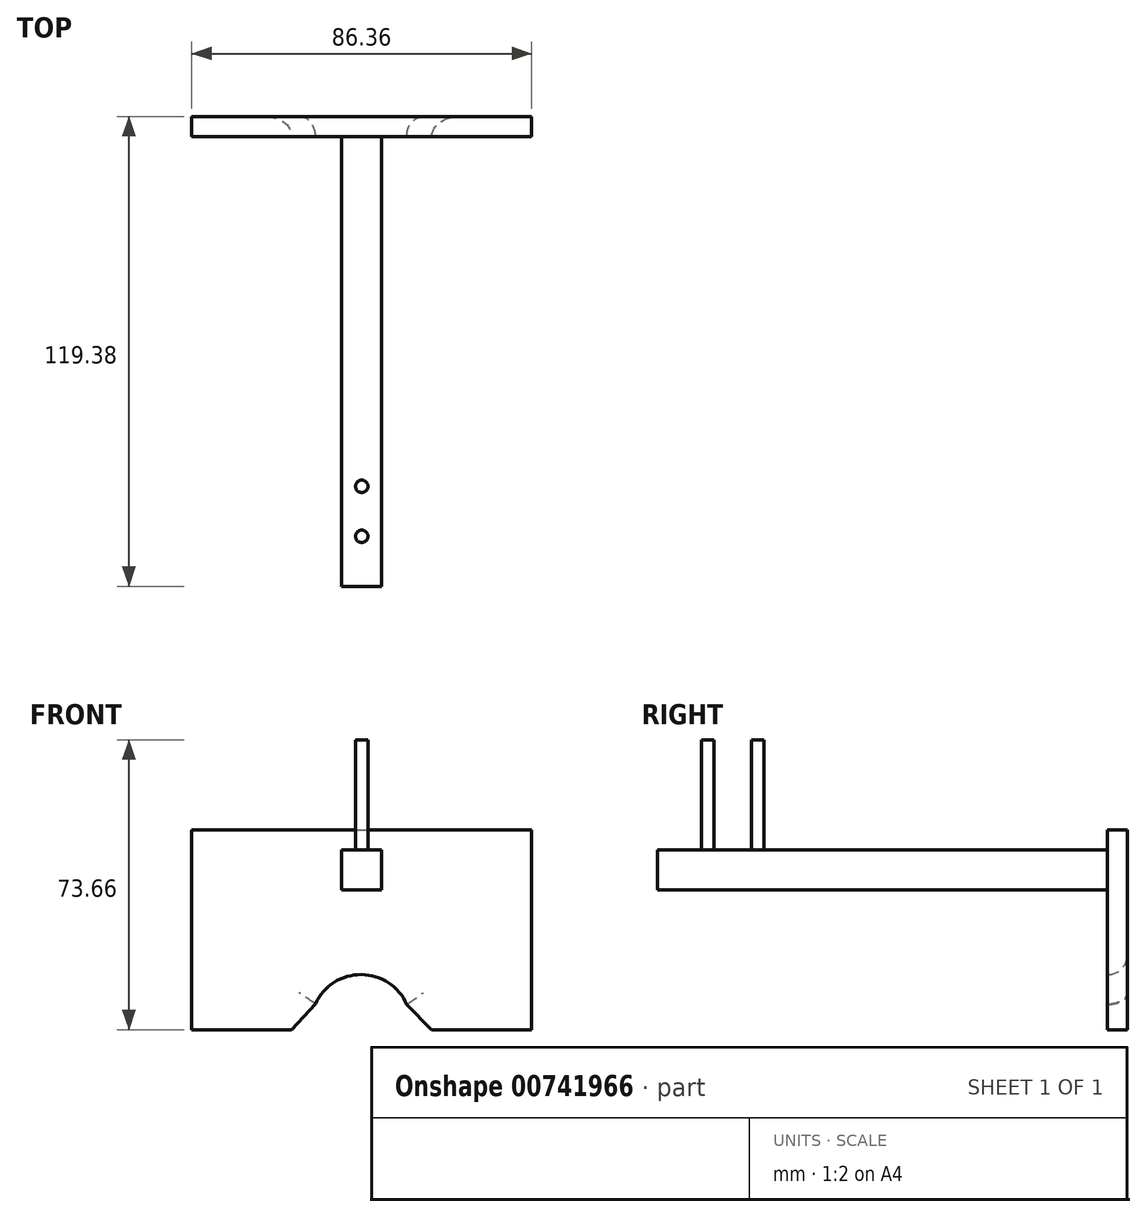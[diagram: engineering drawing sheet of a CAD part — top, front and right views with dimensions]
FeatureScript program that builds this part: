
annotation { "Feature Type Name" : "Feature", "Feature Type Description" : "" }
export const myFeature = defineFeature(function(context is Context, id is Id, definition is map)
    precondition{}
    {
        {
            var Q0;
            Q0=qCreatedBy(makeId("Top.planeOp"),FACE);
            var sketch = newSketch(context, id + "F0", { "sketchPlane" : qUnion([Q0])});
            skLineSegment(sketch, "E0.bottom", {"start": v(14.4, 49.34) * mm, "end": v(24.56, 49.34) * mm});
            skLineSegment(sketch, "E0.top", {"start": v(14.4, -64.96) * mm, "end": v(24.56, -64.96) * mm});
            skLineSegment(sketch, "E0.left", {"start": v(14.4, 49.34) * mm, "end": v(14.4, -64.96) * mm});
            skLineSegment(sketch, "E0.right", {"start": v(24.56, 49.34) * mm, "end": v(24.56, -64.96) * mm});
            skLineSegment(sketch, "E1", {"start": v(14.4, 49.34) * mm, "end": v(14.4, 49.34) * mm});
            skPoint(sketch, "E2.centerSnap0", {"position": v(19.48, 49.34) * mm});
            skLineSegment(sketch, "E3", {"start": v(14.4, -7.81) * mm, "end": v(14.4, -64.96) * mm});
            skLineSegment(sketch, "E4", {"start": v(14.4, -7.81) * mm, "end": v(14.4, -39.56) * mm});
            skCircle(sketch, "E5", {"center": v(19.48, -39.56) * mm, "radius": 1.59 * mm});
            skPoint(sketch, "E5.centerSnap0", {"position": v(19.48, -64.96) * mm});
            skLineSegment(sketch, "E6", {"start": v(14.4, -39.56) * mm, "end": v(14.4, -64.96) * mm});
            skCircle(sketch, "E7", {"center": v(19.48, -52.26) * mm, "radius": 1.59 * mm});
            skPoint(sketch, "E7.centerSnap0", {"position": v(14.4, -52.26) * mm});
            skSolve(sketch);
        }
        {
            var Q0;
            Q0 = qSketchRegion(id + "F0", true);
            extrude(context, id + "F1", {"entities" : qUnion([Q0]), "depth" : 10.16 * mm, "offsetDistance" : 25.4 * mm});
        }
        {
            var Q0;
            Q0=makeQuery(id+"F0.imprint","IMPRINT",FACE,{"disambiguationData":[TD([[makeQuery(id+"F0.imprint","IMPRINT",EDGE,{"derivedFrom":sQuery(id+"F0.wireOp",EDGE,"E5")}),1.0]])]});
            var Q1;
            Q1=makeQuery(id+"F0.imprint","IMPRINT",FACE,{"disambiguationData":[TD([[makeQuery(id+"F0.imprint","IMPRINT",EDGE,{"derivedFrom":sQuery(id+"F0.wireOp",EDGE,"E7")}),1.0]])]});
            extrude(context, id + "F2", {"entities" : qUnion([Q0, Q1]), "operationType" : NewBodyOperationType.ADD, "depth" : 38.1 * mm, "offsetDistance" : 25.4 * mm});
        }
        {
            var Q0;
            Q0=makeQuery(id+"F1.opExtrude","SWEPT_FACE",FACE,{"disambiguationData":[OSD([sQuery(id+"F0.wireOp",EDGE,"E0.bottom")])]});
            var sketch = newSketch(context, id + "F3", { "sketchPlane" : qUnion([Q0])});
            skLineSegment(sketch, "E8", {"start": v(-24.56, 10.16) * mm, "end": v(-24.56, 15.24) * mm});
            skLineSegment(sketch, "E9", {"start": v(-24.56, 15.24) * mm, "end": v(-37.26, 15.24) * mm});
            skLineSegment(sketch, "E10", {"start": v(-1.7, -35.56) * mm, "end": v(-1.7, 15.24) * mm});
            skLineSegment(sketch, "E11", {"start": v(-1.7, 15.24) * mm, "end": v(-24.56, 15.24) * mm});
            skLineSegment(sketch, "E12", {"start": v(-1.7, 15.24) * mm, "end": v(-13.76, 15.24) * mm});
            skArc(sketch, "E13", {"start": v(-7.73, -28.97) * mm, "mid": v(-19.38, -21.56) * mm, "end": v(-30.9, -29.15) * mm});
            skPoint(sketch, "E13.startSnap0", {"position": v(-7.73, 15.24) * mm});
            skPoint(sketch, "E13.endSnap0", {"position": v(-30.9, 15.24) * mm});
            skPoint(sketch, "E13.endSnap1", {"position": v(-39.48, -29.15) * mm});
            skLineSegment(sketch, "E14", {"start": v(-7.73, -28.97) * mm, "end": v(-1.7, -35.56) * mm});
            skLineSegment(sketch, "E15", {"start": v(-14.4, 10.16) * mm, "end": v(-1.7, 10.16) * mm});
            skLineSegment(sketch, "E16", {"start": v(-37.26, 15.24) * mm, "end": v(-37.26, -35.56) * mm});
            skLineSegment(sketch, "E17", {"start": v(-30.9, -29.15) * mm, "end": v(-37.26, -35.56) * mm});
            skLineSegment(sketch, "E18", {"start": v(-1.7, -35.56) * mm, "end": v(-37.26, -35.56) * mm});
            skLineSegment(sketch, "E19", {"start": v(-37.26, -35.56) * mm, "end": v(-62.66, -35.56) * mm});
            skLineSegment(sketch, "E20", {"start": v(-62.66, -35.56) * mm, "end": v(-62.66, 15.24) * mm});
            skLineSegment(sketch, "E21", {"start": v(-62.66, 15.24) * mm, "end": v(-37.26, 15.24) * mm});
            skLineSegment(sketch, "E22", {"start": v(-37.26, 15.24) * mm, "end": v(23.7, 15.24) * mm});
            skLineSegment(sketch, "E23", {"start": v(23.7, 15.24) * mm, "end": v(23.7, -35.56) * mm});
            skLineSegment(sketch, "E24", {"start": v(23.7, -35.56) * mm, "end": v(-1.7, -35.56) * mm});
            skSolve(sketch);
        }
        {
            var Q0;
            {var subQ0=sQuery(id+"F3.wireOp",EDGE,"E8");Q0=makeQuery(id+"F3.imprint","IMPRINT",FACE,{"disambiguationData":[TD([[makeQuery(id+"F3.imprint","IMPRINT",EDGE,{"derivedFrom":subQ0}),1.0]])]});}
            var Q1;
            Q1=makeQuery(id+"F3.imprint","IMPRINT",FACE,{"disambiguationData":[TD([[makeQuery(id+"F3.imprint","IMPRINT",EDGE,{"derivedFrom":sQuery(id+"F3.wireOp",EDGE,"E8")}),-1.0]])]});
            var Q2;
            {var subQ1=sQuery(id+"F0.wireOp",EDGE,"E0.bottom");var subQ6=makeQuery(id+"F1.opExtrude","CAP_EDGE",EDGE,{"disambiguationData":[OSD([subQ1])],"isStart":false});Q2=makeQuery(id+"F3.imprint","IMPRINT",FACE,{"disambiguationData":[TD([[makeQuery(id+"F3.imprint","IMPRINT",EDGE,{"derivedFrom":subQ6}),1.0]])]});}
            var Q3;
            Q3=makeQuery(id+"F3.imprint","IMPRINT",FACE,{"disambiguationData":[TD([[makeQuery(id+"F3.imprint","IMPRINT",EDGE,{"derivedFrom":sQuery(id+"F3.wireOp",EDGE,"E16")}),-1.0]])]});
            var Q4;
            {var subQ0=sQuery(id+"F3.wireOp",EDGE,"E23");Q4=makeQuery(id+"F3.imprint","IMPRINT",FACE,{"disambiguationData":[TD([[makeQuery(id+"F3.imprint","IMPRINT",EDGE,{"derivedFrom":subQ0}),-1.0]])]});}
            extrude(context, id + "F4", {"entities" : qUnion([Q0, Q1, Q2, Q3, Q4]), "operationType" : NewBodyOperationType.ADD, "depth" : 5.08 * mm, "offsetDistance" : 25.4 * mm});
        }
        {
            var Q0;
            Q0=makeQuery(id+"F3.imprint","IMPRINT",FACE,{"disambiguationData":[TD([[makeQuery(id+"F3.imprint","IMPRINT",EDGE,{"derivedFrom":sQuery(id+"F3.wireOp",EDGE,"jyZHnx2S-gdhW-vEa2-EduE-zIaH4PNQknWg")}),1.0]])]});
            var Q1;
            {var subQ1=sQuery(id+"F0.wireOp",EDGE,"E0.bottom");var subQ6=makeQuery(id+"F1.opExtrude","CAP_EDGE",EDGE,{"disambiguationData":[OSD([subQ1])],"isStart":true});Q1=makeQuery(id+"F3.imprint","IMPRINT",FACE,{"disambiguationData":[TD([[makeQuery(id+"F3.imprint","IMPRINT",EDGE,{"derivedFrom":subQ6}),-1.0]])]});}
            extrude(context, id + "F5", {"entities" : qUnion([Q0, Q1]), "operationType" : NewBodyOperationType.ADD, "depth" : 3.8 * mm, "offsetDistance" : 25.4 * mm});
        }
        {
            var Q0;
            Q0=makeQuery(id+"F4.opExtrude","CAP_EDGE",EDGE,{"disambiguationData":[OSD([sQuery(id+"F3.wireOp",EDGE,"E13")])],"isStart":false});
            var Q1;
            Q1=makeQuery(id+"F4.opExtrude","CAP_EDGE",EDGE,{"disambiguationData":[OSD([sQuery(id+"F3.wireOp",EDGE,"r1mt1xXz-K9e7-pJoP-m9IR-Y44I43uz97zV")])],"isStart":false});
            var Q2;
            Q2=makeQuery(id+"F4.opExtrude","CAP_EDGE",EDGE,{"disambiguationData":[OSD([sQuery(id+"F3.wireOp",EDGE,"E14")])],"isStart":false});
            var Q3;
            Q3=makeQuery(id+"F4.opExtrude","CAP_EDGE",EDGE,{"disambiguationData":[OSD([sQuery(id+"F3.wireOp",EDGE,"E17")])],"isStart":false});
            fillet(context, id + "F6", {"entities" : qUnion([Q0, Q1, Q2, Q3]), "radius" : 5.08 * mm, "tangentPropagation" : true, "allowEdgeOverflow" : false});
        }
    });
